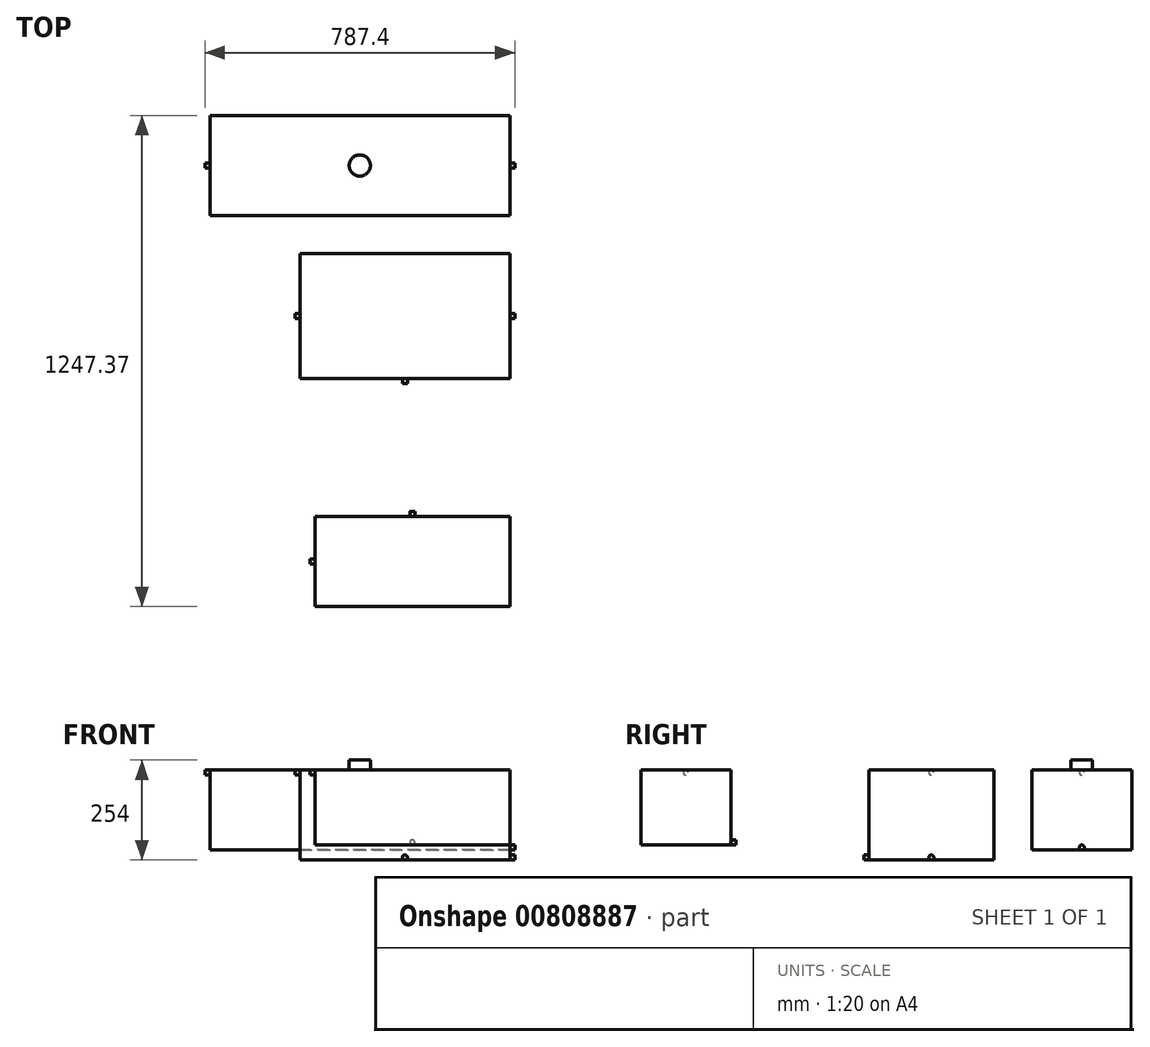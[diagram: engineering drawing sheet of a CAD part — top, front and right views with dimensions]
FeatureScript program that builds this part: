
annotation { "Feature Type Name" : "Feature", "Feature Type Description" : "" }
export const myFeature = defineFeature(function(context is Context, id is Id, definition is map)
    precondition{}
    {
        {
            var Q0;
            Q0=qCreatedBy(makeId("Top.planeOp"),FACE);
            var sketch = newSketch(context, id + "F0", { "sketchPlane" : qUnion([Q0])});
            skLineSegment(sketch, "E0", {"start": v(0, 0) * mm, "end": v(0, -254) * mm});
            skLineSegment(sketch, "E1", {"start": v(0, -254) * mm, "end": v(-762, -254) * mm});
            skLineSegment(sketch, "E2", {"start": v(-762, -254) * mm, "end": v(-762, 0) * mm});
            skLineSegment(sketch, "E3", {"start": v(-762, 0) * mm, "end": v(0, 0) * mm});
            skSolve(sketch);
        }
        {
            var Q0;
            Q0=makeQuery(id+"F0.imprint","IMPRINT",FACE,{"disambiguationData":[TD([[makeQuery(id+"F0.imprint","IMPRINT",EDGE,{"derivedFrom":sQuery(id+"F0.wireOp",EDGE,"E0")}),-1.0]])]});
            extrude(context, id + "F1", {"entities" : qUnion([Q0]), "depth" : -203.2 * mm, "offsetDistance" : 25.4 * mm});
        }
        {
            var Q0;
            Q0=makeQuery(id+"F1.opExtrude","SWEPT_FACE",FACE,{"disambiguationData":[OSD([sQuery(id+"F0.wireOp",EDGE,"E2")])]});
            var sketch = newSketch(context, id + "F2", { "sketchPlane" : qUnion([Q0])});
            skCircle(sketch, "E4", {"center": v(127, -6.35) * mm, "radius": 6.35 * mm});
            skPoint(sketch, "E4.centerSnap0", {"position": v(127, 0) * mm});
            skSolve(sketch);
        }
        {
            var Q0;
            Q0 = qSketchRegion(id + "F2", true);
            extrude(context, id + "F3", {"entities" : qUnion([Q0]), "operationType" : NewBodyOperationType.ADD, "depth" : 12.7 * mm, "offsetDistance" : 25.4 * mm});
        }
        {
            var Q0;
            Q0=makeQuery(id+"F1.opExtrude","SWEPT_FACE",FACE,{"disambiguationData":[OSD([sQuery(id+"F0.wireOp",EDGE,"E0")])]});
            var sketch = newSketch(context, id + "F4", { "sketchPlane" : qUnion([Q0])});
            skCircle(sketch, "E5", {"center": v(-127, -196.85) * mm, "radius": 6.35 * mm});
            skPoint(sketch, "E5.centerSnap0", {"position": v(-127, -203.2) * mm});
            skSolve(sketch);
        }
        {
            var Q0;
            Q0 = qSketchRegion(id + "F4", true);
            extrude(context, id + "F5", {"entities" : qUnion([Q0]), "operationType" : NewBodyOperationType.ADD, "depth" : 12.7 * mm, "offsetDistance" : 25.4 * mm});
        }
        {
            var Q0;
            Q0=qCreatedBy(makeId("Top.planeOp"),FACE);
            var sketch = newSketch(context, id + "F6", { "sketchPlane" : qUnion([Q0])});
            skLineSegment(sketch, "E6", {"start": v(0, -668.04) * mm, "end": v(0, -350.54) * mm});
            skLineSegment(sketch, "E7", {"start": v(0, -350.54) * mm, "end": v(-533.4, -350.54) * mm});
            skLineSegment(sketch, "E8", {"start": v(-533.4, -350.54) * mm, "end": v(-533.4, -668.04) * mm});
            skLineSegment(sketch, "E9", {"start": v(-533.4, -668.04) * mm, "end": v(0, -668.04) * mm});
            skSolve(sketch);
        }
        {
            var Q0;
            Q0=makeQuery(id+"F6.imprint","IMPRINT",FACE,{"disambiguationData":[TD([[makeQuery(id+"F6.imprint","IMPRINT",EDGE,{"derivedFrom":sQuery(id+"F6.wireOp",EDGE,"E6")}),1.0]])]});
            extrude(context, id + "F7", {"entities" : qUnion([Q0]), "depth" : -228.6 * mm, "offsetDistance" : 25.4 * mm});
        }
        {
            var Q0;
            Q0=makeQuery(id+"F7.opExtrude","SWEPT_FACE",FACE,{"disambiguationData":[OSD([sQuery(id+"F6.wireOp",EDGE,"E8")])]});
            var sketch = newSketch(context, id + "F8", { "sketchPlane" : qUnion([Q0])});
            skCircle(sketch, "E10", {"center": v(509.3, -6.35) * mm, "radius": 6.35 * mm});
            skPoint(sketch, "E10.centerSnap0", {"position": v(509.3, 0) * mm});
            skSolve(sketch);
        }
        {
            var Q0;
            Q0 = qSketchRegion(id + "F8", true);
            extrude(context, id + "F9", {"entities" : qUnion([Q0]), "operationType" : NewBodyOperationType.ADD, "depth" : 12.7 * mm, "offsetDistance" : 25.4 * mm});
        }
        {
            var Q0;
            Q0=makeQuery(id+"F7.opExtrude","SWEPT_FACE",FACE,{"disambiguationData":[OSD([sQuery(id+"F6.wireOp",EDGE,"E6")])]});
            var sketch = newSketch(context, id + "F10", { "sketchPlane" : qUnion([Q0])});
            skCircle(sketch, "E11", {"center": v(-509.3, -222.25) * mm, "radius": 6.35 * mm});
            skPoint(sketch, "E11.centerSnap0", {"position": v(-509.3, -228.6) * mm});
            skSolve(sketch);
        }
        {
            var Q0;
            Q0 = qSketchRegion(id + "F10", true);
            extrude(context, id + "F11", {"entities" : qUnion([Q0]), "operationType" : NewBodyOperationType.ADD, "depth" : 12.7 * mm, "offsetDistance" : 25.4 * mm});
        }
        {
            var Q0;
            Q0=makeQuery(id+"F7.opExtrude","SWEPT_FACE",FACE,{"disambiguationData":[OSD([sQuery(id+"F6.wireOp",EDGE,"E9")])]});
            var sketch = newSketch(context, id + "F12", { "sketchPlane" : qUnion([Q0])});
            skCircle(sketch, "E12", {"center": v(-266.7, -222.25) * mm, "radius": 6.35 * mm});
            skPoint(sketch, "E12.centerSnap0", {"position": v(-266.7, -228.6) * mm});
            skSolve(sketch);
        }
        {
            var Q0;
            Q0 = qSketchRegion(id + "F12", true);
            extrude(context, id + "F13", {"entities" : qUnion([Q0]), "operationType" : NewBodyOperationType.ADD, "depth" : 12.7 * mm, "offsetDistance" : 25.4 * mm});
        }
        {
            var Q0;
            Q0=qCreatedBy(makeId("Top.planeOp"),FACE);
            var sketch = newSketch(context, id + "F14", { "sketchPlane" : qUnion([Q0])});
            skLineSegment(sketch, "E13", {"start": v(0, -1018.77) * mm, "end": v(0, -1247.37) * mm});
            skLineSegment(sketch, "E14", {"start": v(0, -1247.37) * mm, "end": v(-495.3, -1247.37) * mm});
            skLineSegment(sketch, "E15", {"start": v(-495.3, -1247.37) * mm, "end": v(-495.3, -1018.77) * mm});
            skLineSegment(sketch, "E16", {"start": v(-495.3, -1018.77) * mm, "end": v(0, -1018.77) * mm});
            skSolve(sketch);
        }
        {
            var Q0;
            Q0=makeQuery(id+"F14.imprint","IMPRINT",FACE,{"disambiguationData":[TD([[makeQuery(id+"F14.imprint","IMPRINT",EDGE,{"derivedFrom":sQuery(id+"F14.wireOp",EDGE,"E13")}),-1.0]])]});
            extrude(context, id + "F15", {"entities" : qUnion([Q0]), "depth" : -190.5 * mm, "offsetDistance" : 25.4 * mm});
        }
        {
            var Q0;
            Q0=makeQuery(id+"F15.opExtrude","SWEPT_FACE",FACE,{"disambiguationData":[OSD([sQuery(id+"F14.wireOp",EDGE,"E15")])]});
            var sketch = newSketch(context, id + "F16", { "sketchPlane" : qUnion([Q0])});
            skCircle(sketch, "E17", {"center": v(1133.07, -6.35) * mm, "radius": 6.35 * mm});
            skPoint(sketch, "E17.centerSnap0", {"position": v(1133.07, 0) * mm});
            skSolve(sketch);
        }
        {
            var Q0;
            Q0 = qSketchRegion(id + "F16", true);
            extrude(context, id + "F17", {"entities" : qUnion([Q0]), "operationType" : NewBodyOperationType.ADD, "depth" : 12.7 * mm, "offsetDistance" : 25.4 * mm});
        }
        {
            var Q0;
            Q0=makeQuery(id+"F15.opExtrude","SWEPT_FACE",FACE,{"disambiguationData":[OSD([sQuery(id+"F14.wireOp",EDGE,"E16")])]});
            var sketch = newSketch(context, id + "F18", { "sketchPlane" : qUnion([Q0])});
            skCircle(sketch, "E18", {"center": v(247.65, -184.15) * mm, "radius": 6.35 * mm});
            skPoint(sketch, "E18.centerSnap0", {"position": v(247.65, -190.5) * mm});
            skSolve(sketch);
        }
        {
            var Q0;
            Q0 = qSketchRegion(id + "F18", true);
            extrude(context, id + "F19", {"entities" : qUnion([Q0]), "operationType" : NewBodyOperationType.ADD, "depth" : 12.7 * mm, "offsetDistance" : 25.4 * mm});
        }
        {
            var Q0;
            Q0=makeQuery(id+"F1.opExtrude","CAP_FACE",FACE,{"disambiguationData":[OSD([sQuery(id+"F0.wireOp",EDGE,"E0"),sQuery(id+"F0.wireOp",EDGE,"E1"),sQuery(id+"F0.wireOp",EDGE,"E2"),sQuery(id+"F0.wireOp",EDGE,"E3")])],"isStart":true});
            var sketch = newSketch(context, id + "F20", { "sketchPlane" : qUnion([Q0])});
            skCircle(sketch, "E19", {"center": v(-381, -127) * mm, "radius": 26.99 * mm});
            skPoint(sketch, "E19.centerSnap0", {"position": v(0, -127) * mm});
            skPoint(sketch, "E19.centerSnap1", {"position": v(-381, 0) * mm});
            skSolve(sketch);
        }
        {
            var Q0;
            Q0 = qSketchRegion(id + "F20", true);
            extrude(context, id + "F21", {"entities" : qUnion([Q0]), "operationType" : NewBodyOperationType.ADD, "depth" : 25.4 * mm, "offsetDistance" : 25.4 * mm});
        }
    });
